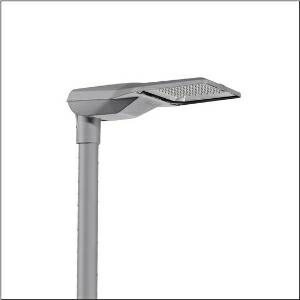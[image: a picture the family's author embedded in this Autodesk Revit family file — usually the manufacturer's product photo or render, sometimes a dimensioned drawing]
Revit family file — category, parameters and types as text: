
# Revit family: streetlight_sl_21_iq_midi___st1_0a_5xe3d31g08nb_2a13
name_source: partatom
category: Lighting Fixtures
units: mm (PartAtom-declared; Revit-internal decimal feet)

## family parameters
Cut with Voids When Loaded = No
Host = Face
Light Source = No
Part Type = Normal
Room Calculation Point = No
Round Connector Dimension = Use Diameter
Shared = No

## types (1)
- --- (1 x LED, 23230 lm, 155.5 W, 3000K)
    Apparent Load = 155 VA
    CIE Flux Codes = 40 73 97 100 100
    Color Rendering = 70
    Color Temperature = 3000K
    Default Elevation = 1800 mm
    Description = Streetlight SL 21 iQ midi, mast luminaire, primary light control with lens, of PMMA, primary optical cover: cover, of toughened safety glass, transparent, light distribution: ST1.0a, light emission: direct distribution, primary light characteristic: asymmetric, installation type: post-top, side-entry, LED, High Power LED, rated luminous flux: 23.230lm, luminous efficacy: 149lm/W, light colour: 730, colour temperature: 3000K, control gear: iQ Street-Remote, control: Street-Remote, Auto-Match, Temp-Guard, Lumen-Switch, Night-Set, Smart-Wire, Light-Fading, Desk-Remote (wireless, voltage-free reading and setting of iQ features in the workshop via application-optimized NFC function/RFID function), optimised constant luminous flux control (CLO 2.0), pre-setting: linear dimming characteristic, mains connection: 230..240V, AC, 50/60Hz, start of lifetime: 156W, end of service life: 162W, reduction: 69W, luminaire housing, of diecast aluminium, powder-coated, Siteco® metallic grey (DB 702S), corrosivity category C5 mid according to DIN EN ISO 12944, please order mast flange separately, inclination adjustable: 0°, 5°, 10°, 15°, sealing non-destructively replaceable, multi-level sealing system, length: 644mm, width: 335mm, height: 110mm, mast flange for spigot size: 42mm (side-entry): 5XC10008XM4, 60/48mm (side-entry/post-top): 5XC10108XM2, 76/60mm (side-entry/post-top): 5XC10108XM1, mounting height: 4..8m, protection rating (complete): IP66, insulation class (complete): insulation class II (safety insulation), certification: CE, ENEC, ENEC+, VDE, impact resistance: IK10, permissible operating ambient temperature for outdoor applications: -40..+50°C, standard-compliant lighting for roads and squares, packaging unit: 1 piece

Light Distribution: ST1.0a
    Height = 111 mm
    Lamp = 1 x LED
    Lamp Light Flux = 23230 lm
    Lamp Power = 155.5 W
    Lamp count = 1
    Length = 644 mm
    Luminous efficacy = 149 lm/W
    Manufacturer = Siteco
    ModVariant = No
    Model = 5XE3D31G08NB
    Number of Poles = 1
    OnlyDefault = Yes
    Power Factor = 1
    Product Name = Streetlight SL 21 iQ midi | ST1.0a
    Product group = mast luminaire | pylon top
    ProductGroupID = 6100
    Protection Class = Protection class II
    Protection Degree = IP 66
    RLX_Detail_Level = 1
    RLX_Emergency_Light_Flux = 0 lm
    RLX_Emergency_Type = 0
    RLX_Emergency_Type_DB = No
    RlxData = <blob elided: 27261 chars, md5=3dc80733>
    Socket = socket
    Standby Power = 0 W
    System Light Flux = 23230 lm
    System Power = 155 W
    Type Comments = factory setting: luminous flux: 100 % | dim-lin: 254 | 823 mA
    Type Image = l_1004298.jpg
    URL = http://relux.com
    VarID = @adj_192315
    Voltage = 0 V
    Weight = 0.00 kg
    Width = 336 mm

## geometry (parser evidence)
native form markers: Blend x4, Sweep x9
no freeform markers — native parametric forms only
